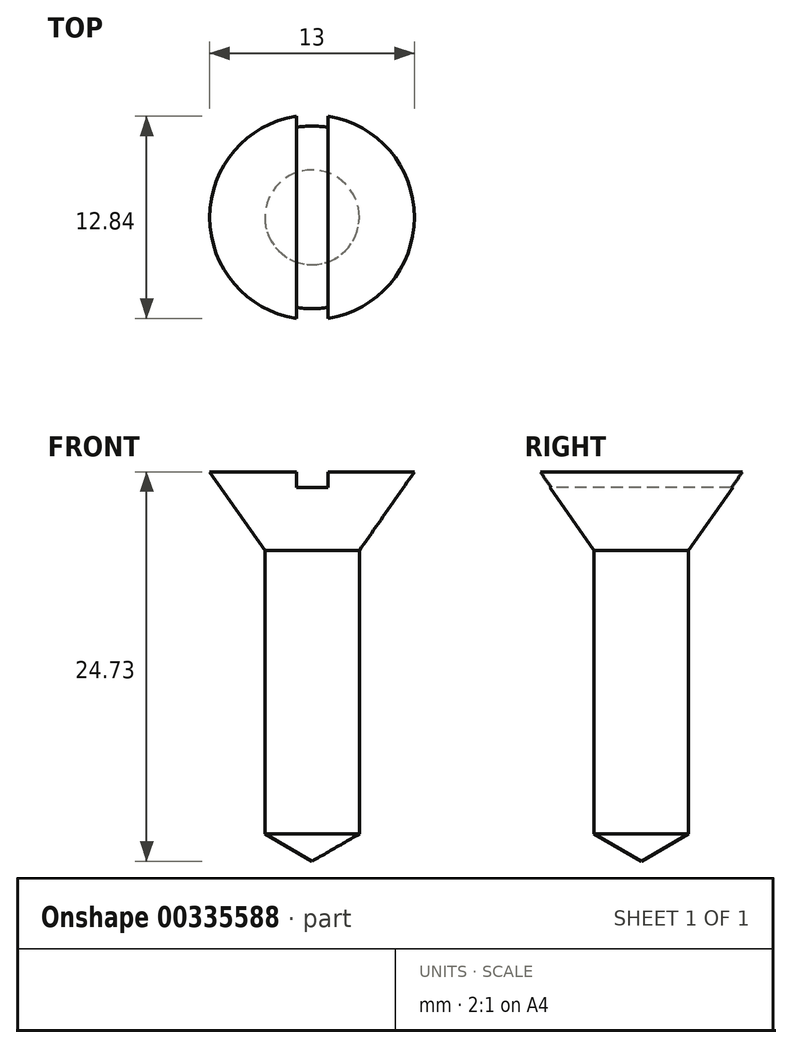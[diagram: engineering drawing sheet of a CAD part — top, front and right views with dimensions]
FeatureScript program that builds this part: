
annotation { "Feature Type Name" : "Feature", "Feature Type Description" : "" }
export const myFeature = defineFeature(function(context is Context, id is Id, definition is map)
    precondition{}
    {
        {
            var Q0;
            Q0=qCreatedBy(makeId("Top.planeOp"),FACE);
            var sketch = newSketch(context, id + "F0", { "sketchPlane" : qUnion([Q0])});
            skCircle(sketch, "E0", {"center": v(0, 0) * mm, "radius": 3 * mm});
            skSolve(sketch);
        }
        {
            var Q0;
            Q0=makeQuery(id+"F0.imprint","IMPRINT",FACE,{"disambiguationData":[TD([[makeQuery(id+"F0.imprint","IMPRINT",EDGE,{"derivedFrom":sQuery(id+"F0.wireOp",EDGE,"E0")}),1.0]])]});
            extrude(context, id + "F1", {"entities" : qUnion([Q0]), "depth" : 18 * mm});
        }
        {
            var Q0;
            Q0=qCreatedBy(makeId("Front.planeOp"),FACE);
            var sketch = newSketch(context, id + "F2", { "sketchPlane" : qUnion([Q0])});
            skLineSegment(sketch, "E1", {"start": v(0, 0) * mm, "end": v(0, -5.31) * mm});
            skLineSegment(sketch, "E2", {"start": v(0, 0) * mm, "end": v(3, 0) * mm});
            skLineSegment(sketch, "E3", {"start": v(3, 0) * mm, "end": v(0, -1.73) * mm});
            skLineSegment(sketch, "E4", {"start": v(0, -1.73) * mm, "end": v(0, 0) * mm});
            skSolve(sketch);
        }
        {
            var Q0;
            Q0=makeQuery(id+"F2.imprint","IMPRINT",FACE,{"disambiguationData":[TD([[makeQuery(id+"F2.imprint","IMPRINT",EDGE,{"derivedFrom":sQuery(id+"F2.wireOp",EDGE,"E2")}),-1.0]])]});
            var Q1;
            Q1=sQuery(id+"F2.wireOp",EDGE,"E4");
            revolve(context, id + "F3", {"entities" : qUnion([Q0]), "axis" : qUnion([Q1]), "revolveType" : RevolveType.FULL});
        }
        {
            var Q0;
            Q0=qCreatedBy(makeId("Front.planeOp"),FACE);
            var sketch = newSketch(context, id + "F4", { "sketchPlane" : qUnion([Q0])});
            skLineSegment(sketch, "E5", {"start": v(0, 0) * mm, "end": v(0, 18) * mm});
            skLineSegment(sketch, "E6", {"start": v(0, 18) * mm, "end": v(-3, 18) * mm});
            skLineSegment(sketch, "E7", {"start": v(0, 18) * mm, "end": v(0, 23) * mm});
            skLineSegment(sketch, "E8", {"start": v(0, 23) * mm, "end": v(-6.5, 23) * mm});
            skLineSegment(sketch, "E9", {"start": v(-6.5, 23) * mm, "end": v(-3, 18) * mm});
            skSolve(sketch);
        }
        {
            var Q0;
            {var subQ2=sQuery(id+"F4.wireOp",EDGE,"E6");Q0=makeQuery(id+"F4.imprint","IMPRINT",FACE,{"disambiguationData":[TD([[makeQuery(id+"F4.imprint","IMPRINT",EDGE,{"derivedFrom":subQ2}),-1.0]])]});}
            var Q1;
            Q1=sQuery(id+"F4.wireOp",EDGE,"E7");
            revolve(context, id + "F5", {"operationType" : NewBodyOperationType.ADD, "entities" : qUnion([Q0]), "axis" : qUnion([Q1]), "revolveType" : RevolveType.FULL});
        }
        {
            var Q0;
            Q0=qCreatedBy(makeId("Front.planeOp"),FACE);
            var sketch = newSketch(context, id + "F6", { "sketchPlane" : qUnion([Q0])});
            skLineSegment(sketch, "E10", {"start": v(0, 0) * mm, "end": v(0, 22) * mm});
            skLineSegment(sketch, "E11", {"start": v(0, 22) * mm, "end": v(-1, 22) * mm});
            skLineSegment(sketch, "E12", {"start": v(-1, 22) * mm, "end": v(-1, 23) * mm});
            skLineSegment(sketch, "E13.MirrorCS", {"start": v(-2, 22) * mm, "end": v(-1, 22) * mm});
            skLineSegment(sketch, "E14", {"start": v(0, 22) * mm, "end": v(1, 22) * mm});
            skLineSegment(sketch, "E15", {"start": v(1, 22) * mm, "end": v(1, 23) * mm});
            skLineSegment(sketch, "E16", {"start": v(-1, 23) * mm, "end": v(1, 23) * mm});
            skSolve(sketch);
        }
        {
            var Q0;
            Q0=qSketchRegion(id+"F6",true);
            extrude(context, id + "F7", {"entities" : qUnion([Q0]), "operationType" : NewBodyOperationType.REMOVE, "endBound" : BoundingType.SYMMETRIC, "oppositeDirection" : true, "depth" : 25 * mm});
        }
    });
